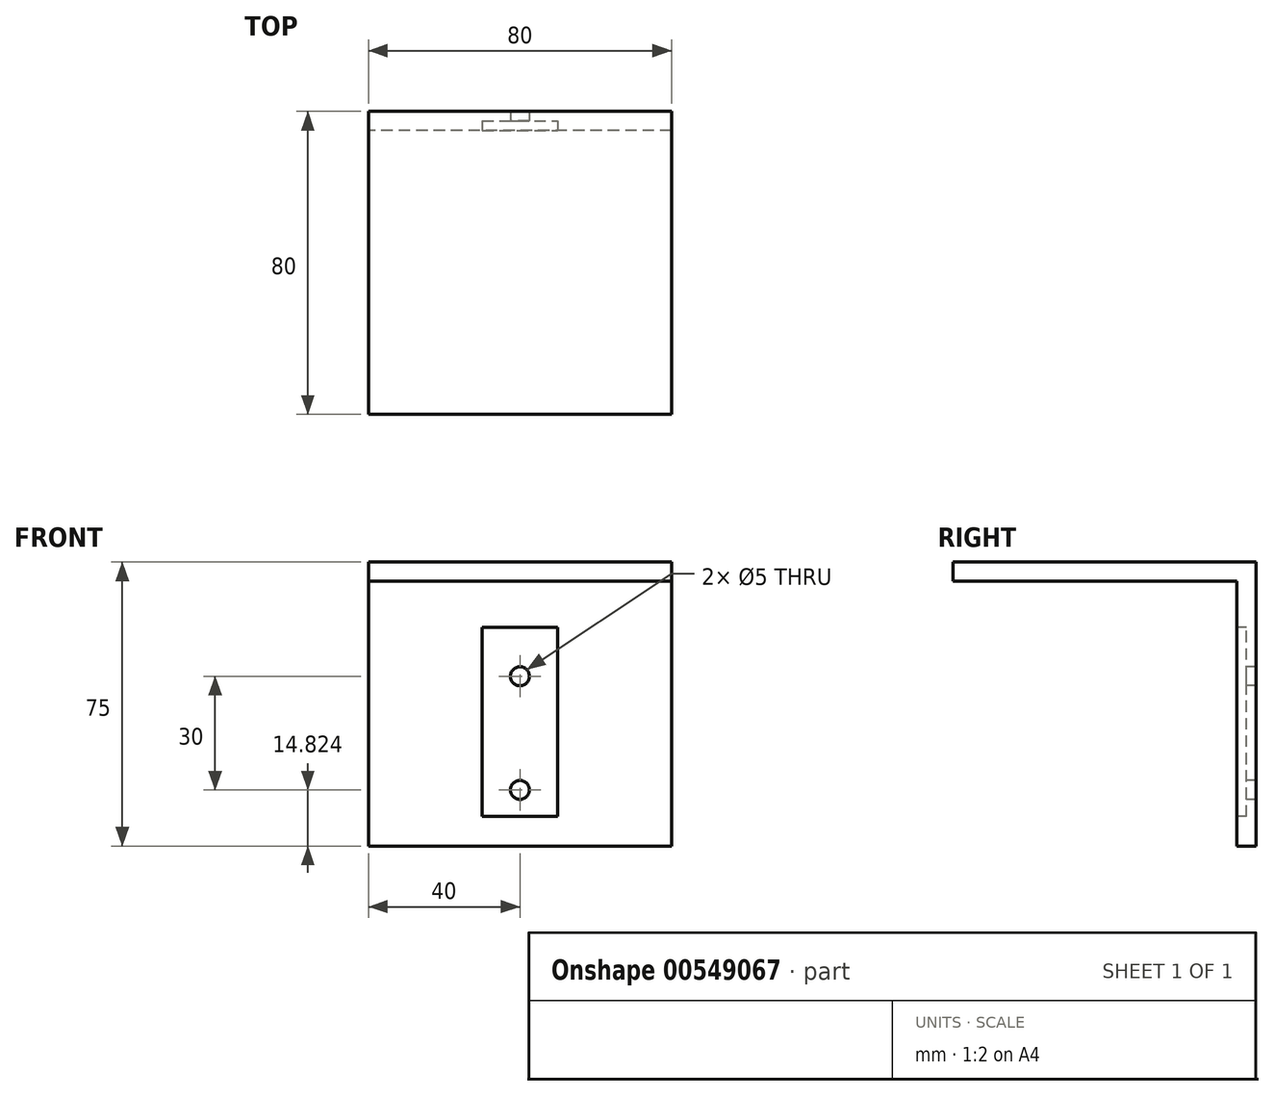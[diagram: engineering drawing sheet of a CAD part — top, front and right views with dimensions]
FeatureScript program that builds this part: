
annotation { "Feature Type Name" : "Feature", "Feature Type Description" : "" }
export const myFeature = defineFeature(function(context is Context, id is Id, definition is map)
    precondition{}
    {
        {
            var Q0;
            Q0=qCreatedBy(makeId("Right.planeOp"),FACE);
            var sketch = newSketch(context, id + "F0", { "sketchPlane" : qUnion([Q0])});
            skLineSegment(sketch, "E0.bottom", {"start": v(-75, 5) * mm, "end": v(0, 5) * mm});
            skLineSegment(sketch, "E0.top", {"start": v(-75, 0) * mm, "end": v(0, 0) * mm});
            skLineSegment(sketch, "E0.left", {"start": v(-75, 5) * mm, "end": v(-75, 0) * mm});
            skLineSegment(sketch, "E0.right", {"start": v(0, 5) * mm, "end": v(0, 0) * mm});
            skLineSegment(sketch, "E1.bottom", {"start": v(0, 5) * mm, "end": v(5, 5) * mm});
            skLineSegment(sketch, "E1.top", {"start": v(0, -70) * mm, "end": v(5, -70) * mm});
            skLineSegment(sketch, "E1.left", {"start": v(0, 5) * mm, "end": v(0, -70) * mm});
            skLineSegment(sketch, "E1.right", {"start": v(5, 5) * mm, "end": v(5, -70) * mm});
            skSolve(sketch);
        }
        {
            var Q0;
            {var subQ0=sQuery(id+"F0.wireOp",EDGE,"E0.bottom");Q0=makeQuery(id+"F0.imprint","IMPRINT",FACE,{"disambiguationData":[TD([[makeQuery(id+"F0.imprint","IMPRINT",EDGE,{"derivedFrom":subQ0}),-1.0]])]});}
            var Q1;
            {var subQ3=sQuery(id+"F0.wireOp",EDGE,"E1.bottom");Q1=makeQuery(id+"F0.imprint","IMPRINT",FACE,{"disambiguationData":[TD([[makeQuery(id+"F0.imprint","IMPRINT",EDGE,{"derivedFrom":subQ3}),-1.0]])]});}
            extrude(context, id + "F1", {"entities" : qUnion([Q0, Q1]), "depth" : 80 * mm, "offsetDistance" : 25 * mm});
        }
        {
            var Q0;
            Q0=qCreatedBy(makeId("Front.planeOp"),FACE);
            var sketch = newSketch(context, id + "F2", { "sketchPlane" : qUnion([Q0])});
            skLineSegment(sketch, "E2.bottom", {"start": v(30, -62.2) * mm, "end": v(50, -62.2) * mm});
            skLineSegment(sketch, "E2.top", {"start": v(30, -12.2) * mm, "end": v(50, -12.2) * mm});
            skLineSegment(sketch, "E2.left", {"start": v(30, -62.2) * mm, "end": v(30, -12.2) * mm});
            skLineSegment(sketch, "E2.right", {"start": v(50, -62.2) * mm, "end": v(50, -12.2) * mm});
            skPoint(sketch, "E2.middle", {"position": v(40, -37.2) * mm});
            skSolve(sketch);
        }
        {
            var Q0;
            Q0=makeQuery(id+"F2.imprint","IMPRINT",FACE,{"disambiguationData":[TD([[makeQuery(id+"F2.imprint","IMPRINT",EDGE,{"derivedFrom":sQuery(id+"F2.wireOp",EDGE,"E2.bottom")}),1.0]])]});
            extrude(context, id + "F3", {"entities" : qUnion([Q0]), "operationType" : NewBodyOperationType.REMOVE, "depth" : -2.5 * mm, "offsetDistance" : 25 * mm});
        }
        {
            var Q0;
            Q0=qCreatedBy(makeId("Front.planeOp"),FACE);
            var sketch = newSketch(context, id + "F4", { "sketchPlane" : qUnion([Q0])});
            skLineSegment(sketch, "E3", {"start": v(5, 4.82) * mm, "end": v(5, -25.18) * mm});
            skLineSegment(sketch, "E4", {"start": v(5, -25.18) * mm, "end": v(5, -55.18) * mm});
            skLineSegment(sketch, "E5", {"start": v(5, -25.18) * mm, "end": v(46.99, -25.18) * mm});
            skLineSegment(sketch, "E6", {"start": v(5, -55.18) * mm, "end": v(44.63, -55.18) * mm});
            skPoint(sketch, "E7", {"position": v(40, -25.18) * mm});
            skPoint(sketch, "E8", {"position": v(40, -55.18) * mm});
            skSolve(sketch);
        }
        {
            var Q0;
            Q0=sQuery(id+"F4.wireOp",VERTEX,"E7");
            var Q1;
            Q1=sQuery(id+"F4.wireOp",VERTEX,"E8");
            var Q2;
            Q2=makeQuery(id+"F1.opExtrude","SWEPT_BODY",BODY,{"disambiguationData":[OSD([sQuery(id+"F0.wireOp",EDGE,"E0.bottom"),sQuery(id+"F0.wireOp",EDGE,"E0.top"),sQuery(id+"F0.wireOp",EDGE,"E0.left"),sQuery(id+"F0.wireOp",EDGE,"E1.bottom"),sQuery(id+"F0.wireOp",EDGE,"E1.top"),sQuery(id+"F0.wireOp",EDGE,"E1.left"),sQuery(id+"F0.wireOp",EDGE,"E1.right")])]});
            hole(context, id + "F5", {"style" : HoleStyle.SIMPLE, "endStyle" : HoleEndStyle.THROUGH, "holeDiameter" : 5 * mm, "isTappedThrough" : true, "tappedDepth" : 12 * mm, "tapClearance" : 3, "locations" : qUnion([Q0, Q1]), "scope" : qUnion([Q2])});
        }
    });
